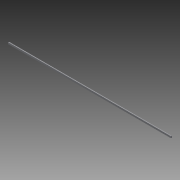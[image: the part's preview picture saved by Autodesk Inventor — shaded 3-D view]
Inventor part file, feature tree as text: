
AUTODESK INVENTOR PART (.ipt)
format: ipt  version: 2013 (Build 170138000, 138)  size: 67,072 bytes
history: native  units: in
note: dims shown in document units (in); Inventor stores cm internally (conversion verified against a paired STEP export)
features: extrude x1, sketch x1
ambient origin geometry x8: Origin, YZ Plane, XZ Plane, XY Plane, X Axis, Y Axis, Z Axis, Center Point
bodies: Solid1 (feature_tree)
feature tree (2):
  extrude  "Extrusion1"  Depth=0.375in
  sketch  "Sketch1"  dims[d0=0.625in d1=0.375in d2=72.0in d3=0.0in]
